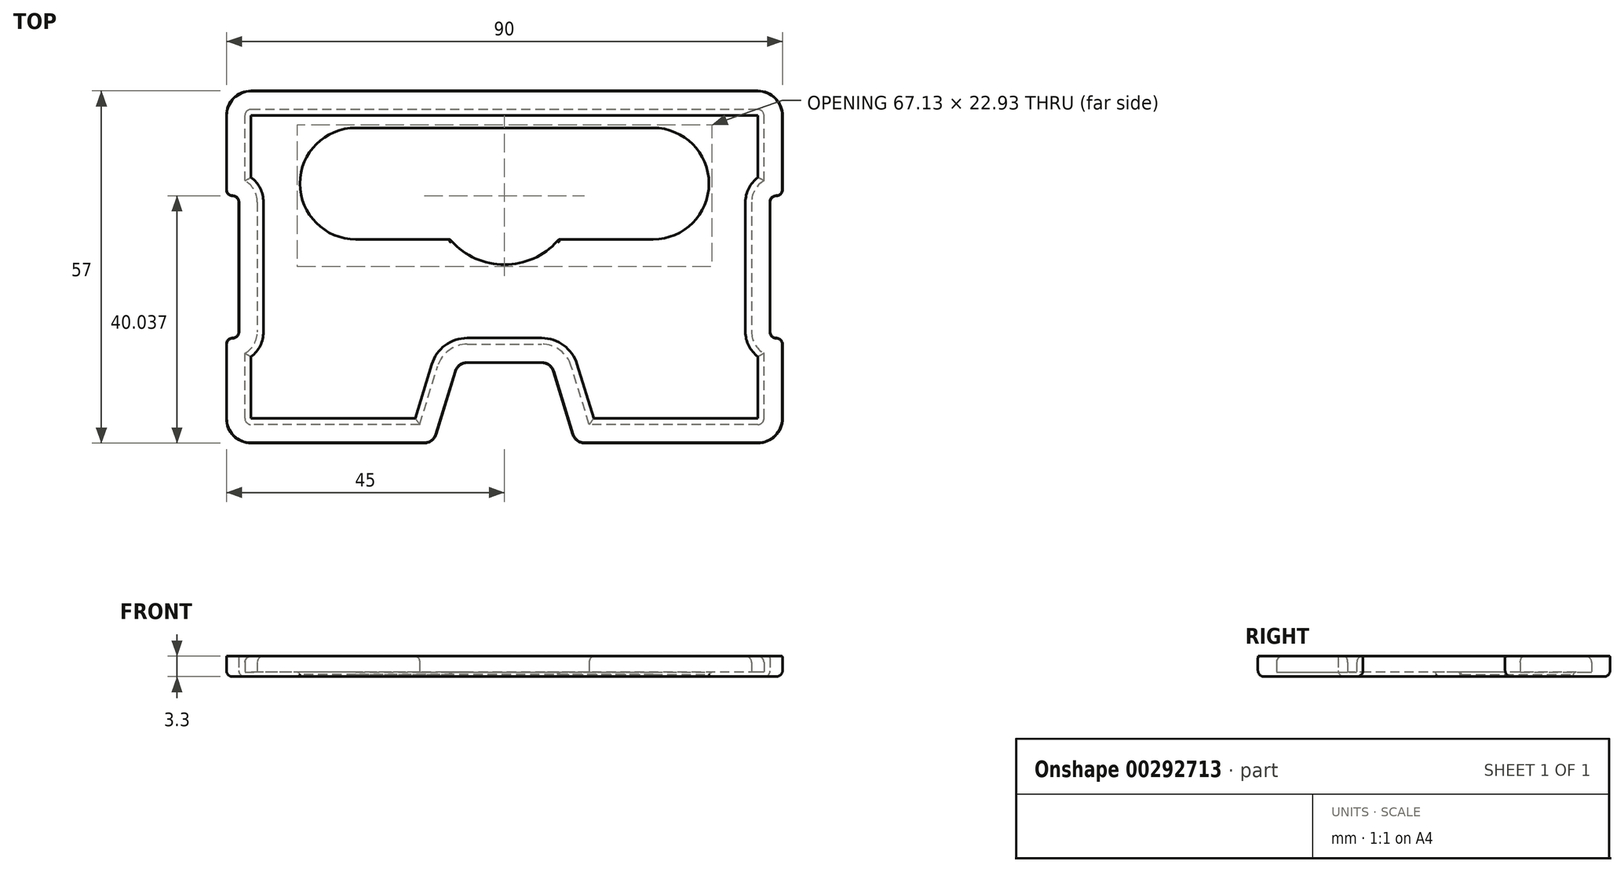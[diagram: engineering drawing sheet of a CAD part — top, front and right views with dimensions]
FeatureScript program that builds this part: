
annotation { "Feature Type Name" : "Feature", "Feature Type Description" : "" }
export const myFeature = defineFeature(function(context is Context, id is Id, definition is map)
    precondition{}
    {
        {
            var Q0;
            Q0=qCreatedBy(makeId("Top.planeOp"),FACE);
            var sketch = newSketch(context, id + "F0", { "sketchPlane" : qUnion([Q0])});
            skLineSegment(sketch, "E0.bottom", {"start": v(41, -28.5) * mm, "end": v(12.98, -28.5) * mm});
            skLineSegment(sketch, "E0.top", {"start": v(41, 28.5) * mm, "end": v(-41, 28.5) * mm});
            skLineSegment(sketch, "E0.left", {"start": v(45, -24.5) * mm, "end": v(45, -12.5) * mm});
            skLineSegment(sketch, "E0.right", {"start": v(-45, -24.5) * mm, "end": v(-45, -12.5) * mm});
            skPoint(sketch, "E0.middle", {"position": v(0, 0) * mm});
            skLineSegment(sketch, "E1.bottom", {"start": v(-44, 11.5) * mm, "end": v(-44, 11.5) * mm});
            skLineSegment(sketch, "E1.top", {"start": v(-44, -11.5) * mm, "end": v(-44, -11.5) * mm});
            skLineSegment(sketch, "E1.right", {"start": v(-43, 10.5) * mm, "end": v(-43, -10.5) * mm});
            skLineSegment(sketch, "E2.bottom", {"start": v(44, 11.5) * mm, "end": v(44, 11.5) * mm});
            skLineSegment(sketch, "E2.top", {"start": v(44, -11.5) * mm, "end": v(44, -11.5) * mm});
            skLineSegment(sketch, "E2.right", {"start": v(43, 10.5) * mm, "end": v(43, -10.5) * mm});
            skLineSegment(sketch, "E3", {"start": v(-45, 12.5) * mm, "end": v(-45, 24.5) * mm});
            skLineSegment(sketch, "E4", {"start": v(45, 12.5) * mm, "end": v(45, 24.5) * mm});
            skLineSegment(sketch, "E5", {"start": v(-12.98, -28.5) * mm, "end": v(-41, -28.5) * mm});
            skPoint(sketch, "E6.visualSharp", {"position": v(45, 28.5) * mm});
            skArc(sketch, "E6.filletArc", {"start": v(45, 24.5) * mm, "mid": v(43.83, 27.33) * mm, "end": v(41, 28.5) * mm});
            skPoint(sketch, "E7.visualSharp", {"position": v(-45, 28.5) * mm});
            skArc(sketch, "E7.filletArc", {"start": v(-41, 28.5) * mm, "mid": v(-43.83, 27.33) * mm, "end": v(-45, 24.5) * mm});
            skPoint(sketch, "E8.visualSharp", {"position": v(-45, -28.5) * mm});
            skArc(sketch, "E8.filletArc", {"start": v(-45, -24.5) * mm, "mid": v(-43.83, -27.33) * mm, "end": v(-41, -28.5) * mm});
            skPoint(sketch, "E9.visualSharp", {"position": v(45, -28.5) * mm});
            skArc(sketch, "E9.filletArc", {"start": v(41, -28.5) * mm, "mid": v(43.83, -27.33) * mm, "end": v(45, -24.5) * mm});
            skPoint(sketch, "E10.visualSharp", {"position": v(-43, 11.5) * mm});
            skArc(sketch, "E10.filletArc", {"start": v(-43, 10.5) * mm, "mid": v(-43.3, 11.2) * mm, "end": v(-44, 11.5) * mm});
            skPoint(sketch, "E11.visualSharp", {"position": v(-43, -11.5) * mm});
            skArc(sketch, "E11.filletArc", {"start": v(-44, -11.5) * mm, "mid": v(-43.3, -11.2) * mm, "end": v(-43, -10.5) * mm});
            skPoint(sketch, "E12.visualSharp", {"position": v(43, 11.5) * mm});
            skArc(sketch, "E12.filletArc", {"start": v(44, 11.5) * mm, "mid": v(43.3, 11.2) * mm, "end": v(43, 10.5) * mm});
            skPoint(sketch, "E13.visualSharp", {"position": v(43, -11.5) * mm});
            skArc(sketch, "E13.filletArc", {"start": v(43, -10.5) * mm, "mid": v(43.3, -11.2) * mm, "end": v(44, -11.5) * mm});
            skPoint(sketch, "E14.visualSharp", {"position": v(-45, 11.5) * mm});
            skArc(sketch, "E14.filletArc", {"start": v(-45, 12.5) * mm, "mid": v(-44.7, 11.8) * mm, "end": v(-44, 11.5) * mm});
            skPoint(sketch, "E15.visualSharp", {"position": v(-45, -11.5) * mm});
            skArc(sketch, "E15.filletArc", {"start": v(-44, -11.5) * mm, "mid": v(-44.7, -11.8) * mm, "end": v(-45, -12.5) * mm});
            skPoint(sketch, "E16.visualSharp", {"position": v(45, 11.5) * mm});
            skArc(sketch, "E16.filletArc", {"start": v(44, 11.5) * mm, "mid": v(44.7, 11.8) * mm, "end": v(45, 12.5) * mm});
            skPoint(sketch, "E17.visualSharp", {"position": v(45, -11.5) * mm});
            skArc(sketch, "E17.filletArc", {"start": v(45, -12.5) * mm, "mid": v(44.7, -11.8) * mm, "end": v(44, -11.5) * mm});
            skLineSegment(sketch, "E18", {"start": v(-11.5, -28.5) * mm, "end": v(-11.5, -15.5) * mm, "construction": true});
            skLineSegment(sketch, "E19", {"start": v(-11.5, -15.5) * mm, "end": v(-7.5, -15.5) * mm, "construction": true});
            skLineSegment(sketch, "E20", {"start": v(-6.02, -15.5) * mm, "end": v(6.02, -15.5) * mm});
            skLineSegment(sketch, "E21", {"start": v(7.5, -15.5) * mm, "end": v(11.5, -15.5) * mm, "construction": true});
            skLineSegment(sketch, "E22", {"start": v(11.5, -15.5) * mm, "end": v(11.5, -28.5) * mm, "construction": true});
            skLineSegment(sketch, "E23", {"start": v(-11.07, -27.09) * mm, "end": v(-7.93, -16.91) * mm});
            skLineSegment(sketch, "E24", {"start": v(11.07, -27.09) * mm, "end": v(7.93, -16.91) * mm});
            skPoint(sketch, "E25.visualSharp", {"position": v(-11.5, -28.5) * mm});
            skArc(sketch, "E25.filletArc", {"start": v(-12.98, -28.5) * mm, "mid": v(-11.79, -28.1) * mm, "end": v(-11.07, -27.09) * mm});
            skPoint(sketch, "E26.visualSharp", {"position": v(11.5, -28.5) * mm});
            skArc(sketch, "E26.filletArc", {"start": v(11.07, -27.09) * mm, "mid": v(11.79, -28.1) * mm, "end": v(12.98, -28.5) * mm});
            skPoint(sketch, "E27.visualSharp", {"position": v(-7.5, -15.5) * mm});
            skArc(sketch, "E27.filletArc", {"start": v(-6.02, -15.5) * mm, "mid": v(-7.21, -15.9) * mm, "end": v(-7.93, -16.91) * mm});
            skPoint(sketch, "E28.visualSharp", {"position": v(7.5, -15.5) * mm});
            skArc(sketch, "E28.filletArc", {"start": v(7.93, -16.91) * mm, "mid": v(7.21, -15.9) * mm, "end": v(6.02, -15.5) * mm});
            skArc(sketch, "E29.11", {"start": v(42.5, 13.66) * mm, "mid": v(41.04, 12.37) * mm, "end": v(40.5, 10.5) * mm, "construction": true});
            skArc(sketch, "E29.20", {"start": v(42.5, 24.5) * mm, "mid": v(42.06, 25.56) * mm, "end": v(41, 26) * mm});
            skArc(sketch, "E30.0", {"start": v(-40, 10.5) * mm, "mid": v(-40.54, 12.5) * mm, "end": v(-42, 13.96) * mm});
            skLineSegment(sketch, "E30.1", {"start": v(-40, 10.5) * mm, "end": v(-40, -10.5) * mm});
            skArc(sketch, "E30.2", {"start": v(-42, -13.96) * mm, "mid": v(-40.54, -12.5) * mm, "end": v(-40, -10.5) * mm});
            skLineSegment(sketch, "E30.3", {"start": v(-42, -24.5) * mm, "end": v(-42, -13.96) * mm});
            skArc(sketch, "E30.4", {"start": v(-42, -24.5) * mm, "mid": v(-41.7, -25.2) * mm, "end": v(-41, -25.5) * mm});
            skLineSegment(sketch, "E30.5", {"start": v(-42, 13.96) * mm, "end": v(-42, 24.5) * mm});
            skLineSegment(sketch, "E30.6", {"start": v(-13.72, -25.5) * mm, "end": v(-41, -25.5) * mm});
            skLineSegment(sketch, "E30.7", {"start": v(-13.72, -25.5) * mm, "end": v(-10.8, -16.03) * mm});
            skArc(sketch, "E30.8", {"start": v(-6.02, -12.5) * mm, "mid": v(-9, -13.48) * mm, "end": v(-10.8, -16.03) * mm});
            skLineSegment(sketch, "E30.9", {"start": v(-6.02, -12.5) * mm, "end": v(6.02, -12.5) * mm});
            skArc(sketch, "E30.10", {"start": v(10.8, -16.03) * mm, "mid": v(9, -13.48) * mm, "end": v(6.02, -12.5) * mm});
            skLineSegment(sketch, "E30.11", {"start": v(13.72, -25.5) * mm, "end": v(10.8, -16.03) * mm});
            skLineSegment(sketch, "E30.12", {"start": v(42, 13.96) * mm, "end": v(42, 24.5) * mm});
            skArc(sketch, "E30.13", {"start": v(42, 24.5) * mm, "mid": v(41.7, 25.2) * mm, "end": v(41, 25.5) * mm});
            skLineSegment(sketch, "E30.14", {"start": v(41, 25.5) * mm, "end": v(-41, 25.5) * mm});
            skArc(sketch, "E30.15", {"start": v(-41, 25.5) * mm, "mid": v(-41.7, 25.2) * mm, "end": v(-42, 24.5) * mm});
            skArc(sketch, "E30.16", {"start": v(42, 13.96) * mm, "mid": v(40.54, 12.5) * mm, "end": v(40, 10.5) * mm});
            skLineSegment(sketch, "E30.17", {"start": v(40, 10.5) * mm, "end": v(40, -10.5) * mm});
            skArc(sketch, "E30.18", {"start": v(40, -10.5) * mm, "mid": v(40.54, -12.5) * mm, "end": v(42, -13.96) * mm});
            skLineSegment(sketch, "E30.19", {"start": v(42, -24.5) * mm, "end": v(42, -13.96) * mm});
            skArc(sketch, "E30.20", {"start": v(41, -25.5) * mm, "mid": v(41.7, -25.2) * mm, "end": v(42, -24.5) * mm});
            skLineSegment(sketch, "E30.21", {"start": v(41, -25.5) * mm, "end": v(13.72, -25.5) * mm});
            skLineSegment(sketch, "E31.bottom", {"start": v(-24.06, 22.5) * mm, "end": v(24.06, 22.5) * mm});
            skLineSegment(sketch, "E31.top", {"start": v(-24.06, 4.5) * mm, "end": v(24.06, 4.5) * mm});
            skLineSegment(sketch, "E31.left", {"start": v(-24.06, 22.5) * mm, "end": v(-24.06, 4.5) * mm, "construction": true});
            skLineSegment(sketch, "E31.right", {"start": v(24.06, 22.5) * mm, "end": v(24.06, 4.5) * mm, "construction": true});
            skCircle(sketch, "E32", {"center": v(-24.06, 13.5) * mm, "radius": 9 * mm});
            skCircle(sketch, "E33", {"center": v(24.06, 13.5) * mm, "radius": 9 * mm});
            skArc(sketch, "E34", {"start": v(-8.83, 4.5) * mm, "mid": v(0, 0.37) * mm, "end": v(8.83, 4.5) * mm});
            skPoint(sketch, "E35", {"position": v(0, 22.5) * mm});
            skLineSegment(sketch, "E36", {"start": v(0, 44.05) * mm, "end": v(0, -36.18) * mm, "construction": true});
            skPoint(sketch, "E37", {"position": v(0, 3.93) * mm});
            skPoint(sketch, "E38", {"position": v(-8.83, 4.5) * mm});
            skPoint(sketch, "E39", {"position": v(8.83, 4.5) * mm});
            skSolve(sketch);
        }
        {
            var Q0;
            Q0=makeQuery(id+"F0.imprint","IMPRINT",FACE,{"disambiguationData":[TD([[makeQuery(id+"F0.imprint","IMPRINT",EDGE,{"derivedFrom":sQuery(id+"F0.wireOp",EDGE,"E0.bottom")}),-1.0]])]});
            extrude(context, id + "F1", {"entities" : qUnion([Q0]), "depth" : 4 * mm, "offsetDistance" : 25 * mm});
        }
        {
            var Q0;
            Q0=makeQuery(id+"F0.imprint","IMPRINT",FACE,{"disambiguationData":[TD([[makeQuery(id+"F0.imprint","IMPRINT",EDGE,{"derivedFrom":sQuery(id+"F0.wireOp",EDGE,"E30.0")}),-1.0]])]});
            extrude(context, id + "F2", {"entities" : qUnion([Q0]), "operationType" : NewBodyOperationType.ADD, "depth" : 0.7 * mm, "offsetDistance" : 25 * mm});
        }
        {
            var Q0;
            Q0=makeQuery(id+"F1.opExtrude","CAP_FACE",FACE,{"disambiguationData":[OSD([sQuery(id+"F0.wireOp",EDGE,"E0.bottom"),sQuery(id+"F0.wireOp",EDGE,"E0.top"),sQuery(id+"F0.wireOp",EDGE,"E0.left"),sQuery(id+"F0.wireOp",EDGE,"E0.right"),sQuery(id+"F0.wireOp",EDGE,"E1.right"),sQuery(id+"F0.wireOp",EDGE,"E2.right"),sQuery(id+"F0.wireOp",EDGE,"E3"),sQuery(id+"F0.wireOp",EDGE,"E4"),sQuery(id+"F0.wireOp",EDGE,"E5"),sQuery(id+"F0.wireOp",EDGE,"E6.filletArc"),sQuery(id+"F0.wireOp",EDGE,"E7.filletArc"),sQuery(id+"F0.wireOp",EDGE,"E8.filletArc"),sQuery(id+"F0.wireOp",EDGE,"E9.filletArc"),sQuery(id+"F0.wireOp",EDGE,"E10.filletArc"),sQuery(id+"F0.wireOp",EDGE,"E11.filletArc"),sQuery(id+"F0.wireOp",EDGE,"E12.filletArc"),sQuery(id+"F0.wireOp",EDGE,"E13.filletArc"),sQuery(id+"F0.wireOp",EDGE,"E14.filletArc"),sQuery(id+"F0.wireOp",EDGE,"E15.filletArc"),sQuery(id+"F0.wireOp",EDGE,"E16.filletArc"),sQuery(id+"F0.wireOp",EDGE,"E17.filletArc"),sQuery(id+"F0.wireOp",EDGE,"E20"),sQuery(id+"F0.wireOp",EDGE,"E23"),sQuery(id+"F0.wireOp",EDGE,"E24"),sQuery(id+"F0.wireOp",EDGE,"E25.filletArc"),sQuery(id+"F0.wireOp",EDGE,"E26.filletArc"),sQuery(id+"F0.wireOp",EDGE,"E27.filletArc"),sQuery(id+"F0.wireOp",EDGE,"E28.filletArc"),sQuery(id+"F0.wireOp",EDGE,"E30.0"),sQuery(id+"F0.wireOp",EDGE,"E30.1"),sQuery(id+"F0.wireOp",EDGE,"E30.2"),sQuery(id+"F0.wireOp",EDGE,"E30.3"),sQuery(id+"F0.wireOp",EDGE,"E30.4"),sQuery(id+"F0.wireOp",EDGE,"E30.5"),sQuery(id+"F0.wireOp",EDGE,"E30.6"),sQuery(id+"F0.wireOp",EDGE,"E30.7"),sQuery(id+"F0.wireOp",EDGE,"E30.8"),sQuery(id+"F0.wireOp",EDGE,"E30.9"),sQuery(id+"F0.wireOp",EDGE,"E30.10"),sQuery(id+"F0.wireOp",EDGE,"E30.11"),sQuery(id+"F0.wireOp",EDGE,"E30.12"),sQuery(id+"F0.wireOp",EDGE,"E30.13"),sQuery(id+"F0.wireOp",EDGE,"E30.14"),sQuery(id+"F0.wireOp",EDGE,"E30.15"),sQuery(id+"F0.wireOp",EDGE,"E30.16"),sQuery(id+"F0.wireOp",EDGE,"E30.17"),sQuery(id+"F0.wireOp",EDGE,"E30.18"),sQuery(id+"F0.wireOp",EDGE,"E30.19"),sQuery(id+"F0.wireOp",EDGE,"E30.20"),sQuery(id+"F0.wireOp",EDGE,"E30.21")])],"isStart":false});
            var sketch = newSketch(context, id + "F3", { "sketchPlane" : qUnion([Q0])});
            skArc(sketch, "E40.0.0", {"start": v(-44, 11.5) * mm, "mid": v(-43.3, 11.2) * mm, "end": v(-43, 10.5) * mm});
            skLineSegment(sketch, "E40.0.1", {"start": v(-43, 10.5) * mm, "end": v(-43, -10.5) * mm});
            skArc(sketch, "E40.0.2", {"start": v(-43, -10.5) * mm, "mid": v(-43.3, -11.2) * mm, "end": v(-44, -11.5) * mm});
            skArc(sketch, "E40.0.3", {"start": v(-44, -11.5) * mm, "mid": v(-44.7, -11.8) * mm, "end": v(-45, -12.5) * mm});
            skLineSegment(sketch, "E40.0.4", {"start": v(-45, -12.5) * mm, "end": v(-45, -24.5) * mm});
            skArc(sketch, "E40.0.5", {"start": v(-45, -24.5) * mm, "mid": v(-43.83, -27.33) * mm, "end": v(-41, -28.5) * mm});
            skLineSegment(sketch, "E40.0.6", {"start": v(-41, -28.5) * mm, "end": v(-12.98, -28.5) * mm});
            skArc(sketch, "E40.0.7", {"start": v(-12.98, -28.5) * mm, "mid": v(-11.79, -28.1) * mm, "end": v(-11.07, -27.09) * mm});
            skLineSegment(sketch, "E40.0.8", {"start": v(-11.07, -27.09) * mm, "end": v(-7.93, -16.91) * mm});
            skArc(sketch, "E40.0.9", {"start": v(-7.93, -16.91) * mm, "mid": v(-7.21, -15.9) * mm, "end": v(-6.02, -15.5) * mm});
            skLineSegment(sketch, "E40.0.10", {"start": v(-6.02, -15.5) * mm, "end": v(6.02, -15.5) * mm});
            skArc(sketch, "E40.0.11", {"start": v(6.02, -15.5) * mm, "mid": v(7.21, -15.9) * mm, "end": v(7.93, -16.91) * mm});
            skLineSegment(sketch, "E40.0.12", {"start": v(7.93, -16.91) * mm, "end": v(11.07, -27.09) * mm});
            skArc(sketch, "E40.0.13", {"start": v(11.07, -27.09) * mm, "mid": v(11.79, -28.1) * mm, "end": v(12.98, -28.5) * mm});
            skLineSegment(sketch, "E40.0.14", {"start": v(12.98, -28.5) * mm, "end": v(41, -28.5) * mm});
            skArc(sketch, "E40.0.15", {"start": v(41, -28.5) * mm, "mid": v(43.83, -27.33) * mm, "end": v(45, -24.5) * mm});
            skLineSegment(sketch, "E40.0.16", {"start": v(45, -24.5) * mm, "end": v(45, -12.5) * mm});
            skArc(sketch, "E40.0.17", {"start": v(45, -12.5) * mm, "mid": v(44.7, -11.8) * mm, "end": v(44, -11.5) * mm});
            skArc(sketch, "E40.0.18", {"start": v(44, -11.5) * mm, "mid": v(43.3, -11.2) * mm, "end": v(43, -10.5) * mm});
            skLineSegment(sketch, "E40.0.19", {"start": v(43, -10.5) * mm, "end": v(43, 10.5) * mm});
            skArc(sketch, "E40.0.20", {"start": v(43, 10.5) * mm, "mid": v(43.3, 11.2) * mm, "end": v(44, 11.5) * mm});
            skArc(sketch, "E40.0.21", {"start": v(44, 11.5) * mm, "mid": v(44.7, 11.8) * mm, "end": v(45, 12.5) * mm});
            skLineSegment(sketch, "E40.0.22", {"start": v(45, 12.5) * mm, "end": v(45, 24.5) * mm});
            skArc(sketch, "E40.0.23", {"start": v(45, 24.5) * mm, "mid": v(43.83, 27.33) * mm, "end": v(41, 28.5) * mm});
            skLineSegment(sketch, "E40.0.24", {"start": v(41, 28.5) * mm, "end": v(-41, 28.5) * mm});
            skArc(sketch, "E40.0.25", {"start": v(-41, 28.5) * mm, "mid": v(-43.83, 27.33) * mm, "end": v(-45, 24.5) * mm});
            skLineSegment(sketch, "E40.0.26", {"start": v(-45, 24.5) * mm, "end": v(-45, 12.5) * mm});
            skArc(sketch, "E40.0.27", {"start": v(-45, 12.5) * mm, "mid": v(-44.7, 11.8) * mm, "end": v(-44, 11.5) * mm});
            skArc(sketch, "E40.1.0", {"start": v(42, -13.96) * mm, "mid": v(40.54, -12.5) * mm, "end": v(40, -10.5) * mm});
            skLineSegment(sketch, "E40.1.1", {"start": v(40, -10.5) * mm, "end": v(40, 10.5) * mm});
            skArc(sketch, "E40.1.2", {"start": v(40, 10.5) * mm, "mid": v(40.54, 12.5) * mm, "end": v(42, 13.96) * mm});
            skLineSegment(sketch, "E40.1.3", {"start": v(42, 13.96) * mm, "end": v(42, 24.5) * mm});
            skArc(sketch, "E40.1.4", {"start": v(42, 24.5) * mm, "mid": v(41.7, 25.2) * mm, "end": v(41, 25.5) * mm});
            skLineSegment(sketch, "E40.1.5", {"start": v(41, 25.5) * mm, "end": v(-41, 25.5) * mm});
            skArc(sketch, "E40.1.6", {"start": v(-41, 25.5) * mm, "mid": v(-41.7, 25.2) * mm, "end": v(-42, 24.5) * mm});
            skLineSegment(sketch, "E40.1.7", {"start": v(-42, 24.5) * mm, "end": v(-42, 13.96) * mm});
            skArc(sketch, "E40.1.8", {"start": v(-42, 13.96) * mm, "mid": v(-40.54, 12.5) * mm, "end": v(-40, 10.5) * mm});
            skLineSegment(sketch, "E40.1.9", {"start": v(-40, 10.5) * mm, "end": v(-40, -10.5) * mm});
            skArc(sketch, "E40.1.10", {"start": v(-40, -10.5) * mm, "mid": v(-40.54, -12.5) * mm, "end": v(-42, -13.96) * mm});
            skLineSegment(sketch, "E40.1.11", {"start": v(-42, -13.96) * mm, "end": v(-42, -24.5) * mm});
            skArc(sketch, "E40.1.12", {"start": v(-42, -24.5) * mm, "mid": v(-41.7, -25.2) * mm, "end": v(-41, -25.5) * mm});
            skLineSegment(sketch, "E40.1.13", {"start": v(-41, -25.5) * mm, "end": v(-13.72, -25.5) * mm});
            skLineSegment(sketch, "E40.1.14", {"start": v(-13.72, -25.5) * mm, "end": v(-10.8, -16.03) * mm});
            skArc(sketch, "E40.1.15", {"start": v(-10.8, -16.03) * mm, "mid": v(-9, -13.48) * mm, "end": v(-6.02, -12.5) * mm});
            skLineSegment(sketch, "E40.1.16", {"start": v(-6.02, -12.5) * mm, "end": v(6.02, -12.5) * mm});
            skArc(sketch, "E40.1.17", {"start": v(6.02, -12.5) * mm, "mid": v(9, -13.48) * mm, "end": v(10.8, -16.03) * mm});
            skLineSegment(sketch, "E40.1.18", {"start": v(10.8, -16.03) * mm, "end": v(13.72, -25.5) * mm});
            skLineSegment(sketch, "E40.1.19", {"start": v(13.72, -25.5) * mm, "end": v(41, -25.5) * mm});
            skArc(sketch, "E40.1.20", {"start": v(41, -25.5) * mm, "mid": v(41.7, -25.2) * mm, "end": v(42, -24.5) * mm});
            skLineSegment(sketch, "E40.1.21", {"start": v(42, -24.5) * mm, "end": v(42, -13.96) * mm});
            skCircle(sketch, "E41.0", {"center": v(24.06, 13.5) * mm, "radius": 9 * mm});
            skLineSegment(sketch, "E41.1", {"start": v(-24.06, 22.5) * mm, "end": v(24.06, 22.5) * mm});
            skCircle(sketch, "E41.2", {"center": v(-24.06, 13.5) * mm, "radius": 9 * mm});
            skLineSegment(sketch, "E41.3", {"start": v(-24.06, 4.5) * mm, "end": v(24.06, 4.5) * mm});
            skArc(sketch, "E42.0", {"start": v(-8.83, 4.5) * mm, "mid": v(0, 0.37) * mm, "end": v(8.83, 4.5) * mm});
            skSolve(sketch);
        }
        {
            var Q0;
            Q0=makeQuery(id+"F3.imprint","IMPRINT",FACE,{"disambiguationData":[TD([[makeQuery(id+"F3.imprint","IMPRINT",EDGE,{"derivedFrom":sQuery(id+"F3.wireOp",EDGE,"E40.0.0")}),-1.0]])]});
            var Q1;
            Q1=makeQuery(id+"F3.imprint","IMPRINT",FACE,{"disambiguationData":[TD([[makeQuery(id+"F3.imprint","IMPRINT",EDGE,{"derivedFrom":sQuery(id+"F3.wireOp",EDGE,"E40.1.0")}),-1.0]])]});
            extrude(context, id + "F4", {"entities" : qUnion([Q0, Q1]), "operationType" : NewBodyOperationType.ADD, "oppositeDirection" : true, "depth" : 0.7 * mm, "offsetDistance" : 25 * mm});
        }
        {
            var Q0;
            Q0=makeQuery(id+"F2.opExtrude","CAP_EDGE",EDGE,{"disambiguationData":[OSD([sQuery(id+"F0.wireOp",EDGE,"E30.1")])],"isStart":false});
            var Q1;
            Q1=makeQuery(id+"F2.opExtrude","CAP_EDGE",EDGE,{"disambiguationData":[OSD([sQuery(id+"F0.wireOp",EDGE,"E30.5")])],"isStart":false});
            var Q2;
            Q2=makeQuery(id+"F2.opExtrude","CAP_EDGE",EDGE,{"disambiguationData":[OSD([sQuery(id+"F0.wireOp",EDGE,"E30.3")])],"isStart":false});
            var Q3;
            Q3=makeQuery(id+"F1.opExtrude","CAP_EDGE",EDGE,{"disambiguationData":[OSD([sQuery(id+"F0.wireOp",EDGE,"E30.9")])],"isStart":false});
            var Q4;
            Q4=makeQuery(id+"F1.opExtrude","CAP_EDGE",EDGE,{"disambiguationData":[OSD([sQuery(id+"F0.wireOp",EDGE,"E30.6")])],"isStart":false});
            var Q5;
            Q5=makeQuery(id+"F1.opExtrude","CAP_EDGE",EDGE,{"disambiguationData":[OSD([sQuery(id+"F0.wireOp",EDGE,"E30.3")])],"isStart":false});
            var Q6;
            Q6=makeQuery(id+"F1.opExtrude","CAP_EDGE",EDGE,{"disambiguationData":[OSD([sQuery(id+"F0.wireOp",EDGE,"E30.1")])],"isStart":false});
            var Q7;
            Q7=makeQuery(id+"F1.opExtrude","CAP_EDGE",EDGE,{"disambiguationData":[OSD([sQuery(id+"F0.wireOp",EDGE,"E30.5")])],"isStart":false});
            var Q8;
            Q8=makeQuery(id+"F2.opExtrude","CAP_EDGE",EDGE,{"disambiguationData":[OSD([sQuery(id+"F0.wireOp",EDGE,"E30.6")])],"isStart":false});
            var Q9;
            Q9=makeQuery(id+"F2.opExtrude","CAP_EDGE",EDGE,{"disambiguationData":[OSD([sQuery(id+"F0.wireOp",EDGE,"E30.9")])],"isStart":false});
            var Q10;
            Q10=makeQuery(id+"F2.opExtrude","CAP_EDGE",EDGE,{"disambiguationData":[OSD([sQuery(id+"F0.wireOp",EDGE,"E30.21")])],"isStart":false});
            var Q11;
            Q11=makeQuery(id+"F2.opExtrude","CAP_EDGE",EDGE,{"disambiguationData":[OSD([sQuery(id+"F0.wireOp",EDGE,"E30.17")])],"isStart":false});
            var Q12;
            Q12=makeQuery(id+"F2.opExtrude","CAP_EDGE",EDGE,{"disambiguationData":[OSD([sQuery(id+"F0.wireOp",EDGE,"E30.14")])],"isStart":false});
            var Q13;
            Q13=makeQuery(id+"F1.opExtrude","CAP_EDGE",EDGE,{"disambiguationData":[OSD([sQuery(id+"F0.wireOp",EDGE,"E30.17")])],"isStart":false});
            var Q14;
            Q14=makeQuery(id+"F1.opExtrude","CAP_EDGE",EDGE,{"disambiguationData":[OSD([sQuery(id+"F0.wireOp",EDGE,"E30.19")])],"isStart":false});
            var Q15;
            Q15=makeQuery(id+"F4.boolean.opBoolean","INTERSECT",EDGE,{"derivedFrom":[makeQuery(id+"F1.opExtrude","SWEPT_FACE",FACE,{"disambiguationData":[OSD([sQuery(id+"F0.wireOp",EDGE,"E30.12")])]}),makeQuery(id+"F4.opExtrude","CAP_FACE",FACE,{"disambiguationData":[OSD([sQuery(id+"F3.wireOp",EDGE,"E40.0.0"),sQuery(id+"F3.wireOp",EDGE,"E40.0.1"),sQuery(id+"F3.wireOp",EDGE,"E40.0.2"),sQuery(id+"F3.wireOp",EDGE,"E40.0.3"),sQuery(id+"F3.wireOp",EDGE,"E40.0.4"),sQuery(id+"F3.wireOp",EDGE,"E40.0.5"),sQuery(id+"F3.wireOp",EDGE,"E40.0.6"),sQuery(id+"F3.wireOp",EDGE,"E40.0.7"),sQuery(id+"F3.wireOp",EDGE,"E40.0.8"),sQuery(id+"F3.wireOp",EDGE,"E40.0.9"),sQuery(id+"F3.wireOp",EDGE,"E40.0.10"),sQuery(id+"F3.wireOp",EDGE,"E40.0.11"),sQuery(id+"F3.wireOp",EDGE,"E40.0.12"),sQuery(id+"F3.wireOp",EDGE,"E40.0.13"),sQuery(id+"F3.wireOp",EDGE,"E40.0.14"),sQuery(id+"F3.wireOp",EDGE,"E40.0.15"),sQuery(id+"F3.wireOp",EDGE,"E40.0.16"),sQuery(id+"F3.wireOp",EDGE,"E40.0.17"),sQuery(id+"F3.wireOp",EDGE,"E40.0.18"),sQuery(id+"F3.wireOp",EDGE,"E40.0.19"),sQuery(id+"F3.wireOp",EDGE,"E40.0.20"),sQuery(id+"F3.wireOp",EDGE,"E40.0.21"),sQuery(id+"F3.wireOp",EDGE,"E40.0.22"),sQuery(id+"F3.wireOp",EDGE,"E40.0.23"),sQuery(id+"F3.wireOp",EDGE,"E40.0.24"),sQuery(id+"F3.wireOp",EDGE,"E40.0.25"),sQuery(id+"F3.wireOp",EDGE,"E40.0.26"),sQuery(id+"F3.wireOp",EDGE,"E40.0.27"),sQuery(id+"F3.wireOp",EDGE,"E41.0"),sQuery(id+"F3.wireOp",EDGE,"E41.1"),sQuery(id+"F3.wireOp",EDGE,"E41.2"),sQuery(id+"F3.wireOp",EDGE,"E41.3"),sQuery(id+"F3.wireOp",EDGE,"E41.4")])],"isStart":false})]});
            var Q16;
            Q16=makeQuery(id+"F4.boolean.opBoolean","INTERSECT",EDGE,{"derivedFrom":[makeQuery(id+"F1.opExtrude","SWEPT_FACE",FACE,{"disambiguationData":[OSD([sQuery(id+"F0.wireOp",EDGE,"E30.17")])]}),makeQuery(id+"F4.opExtrude","CAP_FACE",FACE,{"disambiguationData":[OSD([sQuery(id+"F3.wireOp",EDGE,"E40.0.0"),sQuery(id+"F3.wireOp",EDGE,"E40.0.1"),sQuery(id+"F3.wireOp",EDGE,"E40.0.2"),sQuery(id+"F3.wireOp",EDGE,"E40.0.3"),sQuery(id+"F3.wireOp",EDGE,"E40.0.4"),sQuery(id+"F3.wireOp",EDGE,"E40.0.5"),sQuery(id+"F3.wireOp",EDGE,"E40.0.6"),sQuery(id+"F3.wireOp",EDGE,"E40.0.7"),sQuery(id+"F3.wireOp",EDGE,"E40.0.8"),sQuery(id+"F3.wireOp",EDGE,"E40.0.9"),sQuery(id+"F3.wireOp",EDGE,"E40.0.10"),sQuery(id+"F3.wireOp",EDGE,"E40.0.11"),sQuery(id+"F3.wireOp",EDGE,"E40.0.12"),sQuery(id+"F3.wireOp",EDGE,"E40.0.13"),sQuery(id+"F3.wireOp",EDGE,"E40.0.14"),sQuery(id+"F3.wireOp",EDGE,"E40.0.15"),sQuery(id+"F3.wireOp",EDGE,"E40.0.16"),sQuery(id+"F3.wireOp",EDGE,"E40.0.17"),sQuery(id+"F3.wireOp",EDGE,"E40.0.18"),sQuery(id+"F3.wireOp",EDGE,"E40.0.19"),sQuery(id+"F3.wireOp",EDGE,"E40.0.20"),sQuery(id+"F3.wireOp",EDGE,"E40.0.21"),sQuery(id+"F3.wireOp",EDGE,"E40.0.22"),sQuery(id+"F3.wireOp",EDGE,"E40.0.23"),sQuery(id+"F3.wireOp",EDGE,"E40.0.24"),sQuery(id+"F3.wireOp",EDGE,"E40.0.25"),sQuery(id+"F3.wireOp",EDGE,"E40.0.26"),sQuery(id+"F3.wireOp",EDGE,"E40.0.27"),sQuery(id+"F3.wireOp",EDGE,"E41.0"),sQuery(id+"F3.wireOp",EDGE,"E41.1"),sQuery(id+"F3.wireOp",EDGE,"E41.2"),sQuery(id+"F3.wireOp",EDGE,"E41.3"),sQuery(id+"F3.wireOp",EDGE,"E41.4")])],"isStart":false})]});
            var Q17;
            Q17=makeQuery(id+"F4.boolean.opBoolean","INTERSECT",EDGE,{"derivedFrom":[makeQuery(id+"F1.opExtrude","SWEPT_FACE",FACE,{"disambiguationData":[OSD([sQuery(id+"F0.wireOp",EDGE,"E30.19")])]}),makeQuery(id+"F4.opExtrude","CAP_FACE",FACE,{"disambiguationData":[OSD([sQuery(id+"F3.wireOp",EDGE,"E40.0.0"),sQuery(id+"F3.wireOp",EDGE,"E40.0.1"),sQuery(id+"F3.wireOp",EDGE,"E40.0.2"),sQuery(id+"F3.wireOp",EDGE,"E40.0.3"),sQuery(id+"F3.wireOp",EDGE,"E40.0.4"),sQuery(id+"F3.wireOp",EDGE,"E40.0.5"),sQuery(id+"F3.wireOp",EDGE,"E40.0.6"),sQuery(id+"F3.wireOp",EDGE,"E40.0.7"),sQuery(id+"F3.wireOp",EDGE,"E40.0.8"),sQuery(id+"F3.wireOp",EDGE,"E40.0.9"),sQuery(id+"F3.wireOp",EDGE,"E40.0.10"),sQuery(id+"F3.wireOp",EDGE,"E40.0.11"),sQuery(id+"F3.wireOp",EDGE,"E40.0.12"),sQuery(id+"F3.wireOp",EDGE,"E40.0.13"),sQuery(id+"F3.wireOp",EDGE,"E40.0.14"),sQuery(id+"F3.wireOp",EDGE,"E40.0.15"),sQuery(id+"F3.wireOp",EDGE,"E40.0.16"),sQuery(id+"F3.wireOp",EDGE,"E40.0.17"),sQuery(id+"F3.wireOp",EDGE,"E40.0.18"),sQuery(id+"F3.wireOp",EDGE,"E40.0.19"),sQuery(id+"F3.wireOp",EDGE,"E40.0.20"),sQuery(id+"F3.wireOp",EDGE,"E40.0.21"),sQuery(id+"F3.wireOp",EDGE,"E40.0.22"),sQuery(id+"F3.wireOp",EDGE,"E40.0.23"),sQuery(id+"F3.wireOp",EDGE,"E40.0.24"),sQuery(id+"F3.wireOp",EDGE,"E40.0.25"),sQuery(id+"F3.wireOp",EDGE,"E40.0.26"),sQuery(id+"F3.wireOp",EDGE,"E40.0.27"),sQuery(id+"F3.wireOp",EDGE,"E41.0"),sQuery(id+"F3.wireOp",EDGE,"E41.1"),sQuery(id+"F3.wireOp",EDGE,"E41.2"),sQuery(id+"F3.wireOp",EDGE,"E41.3"),sQuery(id+"F3.wireOp",EDGE,"E41.4")])],"isStart":false})]});
            var Q18;
            Q18=makeQuery(id+"F4.boolean.opBoolean","INTERSECT",EDGE,{"derivedFrom":[makeQuery(id+"F1.opExtrude","SWEPT_FACE",FACE,{"disambiguationData":[OSD([sQuery(id+"F0.wireOp",EDGE,"E30.21")])]}),makeQuery(id+"F4.opExtrude","CAP_FACE",FACE,{"disambiguationData":[OSD([sQuery(id+"F3.wireOp",EDGE,"E40.0.0"),sQuery(id+"F3.wireOp",EDGE,"E40.0.1"),sQuery(id+"F3.wireOp",EDGE,"E40.0.2"),sQuery(id+"F3.wireOp",EDGE,"E40.0.3"),sQuery(id+"F3.wireOp",EDGE,"E40.0.4"),sQuery(id+"F3.wireOp",EDGE,"E40.0.5"),sQuery(id+"F3.wireOp",EDGE,"E40.0.6"),sQuery(id+"F3.wireOp",EDGE,"E40.0.7"),sQuery(id+"F3.wireOp",EDGE,"E40.0.8"),sQuery(id+"F3.wireOp",EDGE,"E40.0.9"),sQuery(id+"F3.wireOp",EDGE,"E40.0.10"),sQuery(id+"F3.wireOp",EDGE,"E40.0.11"),sQuery(id+"F3.wireOp",EDGE,"E40.0.12"),sQuery(id+"F3.wireOp",EDGE,"E40.0.13"),sQuery(id+"F3.wireOp",EDGE,"E40.0.14"),sQuery(id+"F3.wireOp",EDGE,"E40.0.15"),sQuery(id+"F3.wireOp",EDGE,"E40.0.16"),sQuery(id+"F3.wireOp",EDGE,"E40.0.17"),sQuery(id+"F3.wireOp",EDGE,"E40.0.18"),sQuery(id+"F3.wireOp",EDGE,"E40.0.19"),sQuery(id+"F3.wireOp",EDGE,"E40.0.20"),sQuery(id+"F3.wireOp",EDGE,"E40.0.21"),sQuery(id+"F3.wireOp",EDGE,"E40.0.22"),sQuery(id+"F3.wireOp",EDGE,"E40.0.23"),sQuery(id+"F3.wireOp",EDGE,"E40.0.24"),sQuery(id+"F3.wireOp",EDGE,"E40.0.25"),sQuery(id+"F3.wireOp",EDGE,"E40.0.26"),sQuery(id+"F3.wireOp",EDGE,"E40.0.27"),sQuery(id+"F3.wireOp",EDGE,"E41.0"),sQuery(id+"F3.wireOp",EDGE,"E41.1"),sQuery(id+"F3.wireOp",EDGE,"E41.2"),sQuery(id+"F3.wireOp",EDGE,"E41.3"),sQuery(id+"F3.wireOp",EDGE,"E41.4")])],"isStart":false})]});
            var Q19;
            Q19=makeQuery(id+"F4.boolean.opBoolean","INTERSECT",EDGE,{"derivedFrom":[makeQuery(id+"F1.opExtrude","SWEPT_FACE",FACE,{"disambiguationData":[OSD([sQuery(id+"F0.wireOp",EDGE,"E30.9")])]}),makeQuery(id+"F4.opExtrude","CAP_FACE",FACE,{"disambiguationData":[OSD([sQuery(id+"F3.wireOp",EDGE,"E40.0.0"),sQuery(id+"F3.wireOp",EDGE,"E40.0.1"),sQuery(id+"F3.wireOp",EDGE,"E40.0.2"),sQuery(id+"F3.wireOp",EDGE,"E40.0.3"),sQuery(id+"F3.wireOp",EDGE,"E40.0.4"),sQuery(id+"F3.wireOp",EDGE,"E40.0.5"),sQuery(id+"F3.wireOp",EDGE,"E40.0.6"),sQuery(id+"F3.wireOp",EDGE,"E40.0.7"),sQuery(id+"F3.wireOp",EDGE,"E40.0.8"),sQuery(id+"F3.wireOp",EDGE,"E40.0.9"),sQuery(id+"F3.wireOp",EDGE,"E40.0.10"),sQuery(id+"F3.wireOp",EDGE,"E40.0.11"),sQuery(id+"F3.wireOp",EDGE,"E40.0.12"),sQuery(id+"F3.wireOp",EDGE,"E40.0.13"),sQuery(id+"F3.wireOp",EDGE,"E40.0.14"),sQuery(id+"F3.wireOp",EDGE,"E40.0.15"),sQuery(id+"F3.wireOp",EDGE,"E40.0.16"),sQuery(id+"F3.wireOp",EDGE,"E40.0.17"),sQuery(id+"F3.wireOp",EDGE,"E40.0.18"),sQuery(id+"F3.wireOp",EDGE,"E40.0.19"),sQuery(id+"F3.wireOp",EDGE,"E40.0.20"),sQuery(id+"F3.wireOp",EDGE,"E40.0.21"),sQuery(id+"F3.wireOp",EDGE,"E40.0.22"),sQuery(id+"F3.wireOp",EDGE,"E40.0.23"),sQuery(id+"F3.wireOp",EDGE,"E40.0.24"),sQuery(id+"F3.wireOp",EDGE,"E40.0.25"),sQuery(id+"F3.wireOp",EDGE,"E40.0.26"),sQuery(id+"F3.wireOp",EDGE,"E40.0.27"),sQuery(id+"F3.wireOp",EDGE,"E41.0"),sQuery(id+"F3.wireOp",EDGE,"E41.1"),sQuery(id+"F3.wireOp",EDGE,"E41.2"),sQuery(id+"F3.wireOp",EDGE,"E41.3"),sQuery(id+"F3.wireOp",EDGE,"E41.4")])],"isStart":false})]});
            var Q20;
            Q20=makeQuery(id+"F4.boolean.opBoolean","INTERSECT",EDGE,{"derivedFrom":[makeQuery(id+"F1.opExtrude","SWEPT_FACE",FACE,{"disambiguationData":[OSD([sQuery(id+"F0.wireOp",EDGE,"E30.6")])]}),makeQuery(id+"F4.opExtrude","CAP_FACE",FACE,{"disambiguationData":[OSD([sQuery(id+"F3.wireOp",EDGE,"E40.0.0"),sQuery(id+"F3.wireOp",EDGE,"E40.0.1"),sQuery(id+"F3.wireOp",EDGE,"E40.0.2"),sQuery(id+"F3.wireOp",EDGE,"E40.0.3"),sQuery(id+"F3.wireOp",EDGE,"E40.0.4"),sQuery(id+"F3.wireOp",EDGE,"E40.0.5"),sQuery(id+"F3.wireOp",EDGE,"E40.0.6"),sQuery(id+"F3.wireOp",EDGE,"E40.0.7"),sQuery(id+"F3.wireOp",EDGE,"E40.0.8"),sQuery(id+"F3.wireOp",EDGE,"E40.0.9"),sQuery(id+"F3.wireOp",EDGE,"E40.0.10"),sQuery(id+"F3.wireOp",EDGE,"E40.0.11"),sQuery(id+"F3.wireOp",EDGE,"E40.0.12"),sQuery(id+"F3.wireOp",EDGE,"E40.0.13"),sQuery(id+"F3.wireOp",EDGE,"E40.0.14"),sQuery(id+"F3.wireOp",EDGE,"E40.0.15"),sQuery(id+"F3.wireOp",EDGE,"E40.0.16"),sQuery(id+"F3.wireOp",EDGE,"E40.0.17"),sQuery(id+"F3.wireOp",EDGE,"E40.0.18"),sQuery(id+"F3.wireOp",EDGE,"E40.0.19"),sQuery(id+"F3.wireOp",EDGE,"E40.0.20"),sQuery(id+"F3.wireOp",EDGE,"E40.0.21"),sQuery(id+"F3.wireOp",EDGE,"E40.0.22"),sQuery(id+"F3.wireOp",EDGE,"E40.0.23"),sQuery(id+"F3.wireOp",EDGE,"E40.0.24"),sQuery(id+"F3.wireOp",EDGE,"E40.0.25"),sQuery(id+"F3.wireOp",EDGE,"E40.0.26"),sQuery(id+"F3.wireOp",EDGE,"E40.0.27"),sQuery(id+"F3.wireOp",EDGE,"E41.0"),sQuery(id+"F3.wireOp",EDGE,"E41.1"),sQuery(id+"F3.wireOp",EDGE,"E41.2"),sQuery(id+"F3.wireOp",EDGE,"E41.3"),sQuery(id+"F3.wireOp",EDGE,"E41.4")])],"isStart":false})]});
            var Q21;
            Q21=makeQuery(id+"F4.boolean.opBoolean","INTERSECT",EDGE,{"derivedFrom":[makeQuery(id+"F1.opExtrude","SWEPT_FACE",FACE,{"disambiguationData":[OSD([sQuery(id+"F0.wireOp",EDGE,"E30.1")])]}),makeQuery(id+"F4.opExtrude","CAP_FACE",FACE,{"disambiguationData":[OSD([sQuery(id+"F3.wireOp",EDGE,"E40.0.0"),sQuery(id+"F3.wireOp",EDGE,"E40.0.1"),sQuery(id+"F3.wireOp",EDGE,"E40.0.2"),sQuery(id+"F3.wireOp",EDGE,"E40.0.3"),sQuery(id+"F3.wireOp",EDGE,"E40.0.4"),sQuery(id+"F3.wireOp",EDGE,"E40.0.5"),sQuery(id+"F3.wireOp",EDGE,"E40.0.6"),sQuery(id+"F3.wireOp",EDGE,"E40.0.7"),sQuery(id+"F3.wireOp",EDGE,"E40.0.8"),sQuery(id+"F3.wireOp",EDGE,"E40.0.9"),sQuery(id+"F3.wireOp",EDGE,"E40.0.10"),sQuery(id+"F3.wireOp",EDGE,"E40.0.11"),sQuery(id+"F3.wireOp",EDGE,"E40.0.12"),sQuery(id+"F3.wireOp",EDGE,"E40.0.13"),sQuery(id+"F3.wireOp",EDGE,"E40.0.14"),sQuery(id+"F3.wireOp",EDGE,"E40.0.15"),sQuery(id+"F3.wireOp",EDGE,"E40.0.16"),sQuery(id+"F3.wireOp",EDGE,"E40.0.17"),sQuery(id+"F3.wireOp",EDGE,"E40.0.18"),sQuery(id+"F3.wireOp",EDGE,"E40.0.19"),sQuery(id+"F3.wireOp",EDGE,"E40.0.20"),sQuery(id+"F3.wireOp",EDGE,"E40.0.21"),sQuery(id+"F3.wireOp",EDGE,"E40.0.22"),sQuery(id+"F3.wireOp",EDGE,"E40.0.23"),sQuery(id+"F3.wireOp",EDGE,"E40.0.24"),sQuery(id+"F3.wireOp",EDGE,"E40.0.25"),sQuery(id+"F3.wireOp",EDGE,"E40.0.26"),sQuery(id+"F3.wireOp",EDGE,"E40.0.27"),sQuery(id+"F3.wireOp",EDGE,"E41.0"),sQuery(id+"F3.wireOp",EDGE,"E41.1"),sQuery(id+"F3.wireOp",EDGE,"E41.2"),sQuery(id+"F3.wireOp",EDGE,"E41.3"),sQuery(id+"F3.wireOp",EDGE,"E41.4")])],"isStart":false})]});
            fillet(context, id + "F5", {"entities" : qUnion([Q0, Q1, Q2, Q3, Q4, Q5, Q6, Q7, Q8, Q9, Q10, Q11, Q12, Q13, Q14, Q15, Q16, Q17, Q18, Q19, Q20, Q21]), "tangentPropagation" : true, "radius" : 1 * mm, "defaultsChanged" : false, "vertexSettings" : [], "allowEdgeOverflow" : false});
        }
        {
            var Q0;
            Q0=makeQuery(id+"F4.opExtrude","CAP_EDGE",EDGE,{"disambiguationData":[OSD([sQuery(id+"F3.wireOp",EDGE,"E40.0.24")])],"isStart":false});
            var Q1;
            Q1=makeQuery(id+"F1.opExtrude","CAP_EDGE",EDGE,{"disambiguationData":[OSD([sQuery(id+"F0.wireOp",EDGE,"E0.top")])],"isStart":true});
            var Q2;
            Q2=makeQuery(id+"F1.opExtrude","CAP_EDGE",EDGE,{"disambiguationData":[OSD([sQuery(id+"F0.wireOp",EDGE,"E0.top")])],"isStart":false});
            fillet(context, id + "F6", {"entities" : qUnion([Q0, Q1, Q2]), "tangentPropagation" : true, "radius" : 1 * mm, "defaultsChanged" : false, "vertexSettings" : [], "allowEdgeOverflow" : false});
        }
        {
            var Q0;
            {var subQ0=sQuery(id+"F3.wireOp",EDGE,"E41.3");Q0=makeQuery(id+"F4.opExtrude","CAP_EDGE",EDGE,{"disambiguationData":[OSD([subQ0]),TDD([makeQuery(id+"F3.imprint","IMPRINT",EDGE,{"disambiguationData":[TD([[makeQuery(id+"F3.imprint","INTERSECT",VERTEX,{"derivedFrom":[sQuery(id+"F3.wireOp",EDGE,"E41.2"),subQ0]}),-1.0]])],"derivedFrom":subQ0})])],"isStart":false});}
            var Q1;
            {var subQ0=sQuery(id+"F0.wireOp",EDGE,"E31.top");Q1=makeQuery(id+"F2.opExtrude","CAP_EDGE",EDGE,{"disambiguationData":[OSD([subQ0]),TDD([makeQuery(id+"F0.imprint","IMPRINT",EDGE,{"disambiguationData":[TD([[makeQuery(id+"F0.imprint","INTERSECT",VERTEX,{"derivedFrom":[subQ0,sQuery(id+"F0.wireOp",EDGE,"E32")]}),-1.0]])],"derivedFrom":subQ0})])],"isStart":false});}
            var Q2;
            {var subQ0=sQuery(id+"F3.wireOp",EDGE,"E41.3");Q2=makeQuery(id+"F4.opExtrude","CAP_EDGE",EDGE,{"disambiguationData":[OSD([subQ0]),TDD([makeQuery(id+"F3.imprint","IMPRINT",EDGE,{"disambiguationData":[TD([[makeQuery(id+"F3.imprint","INTERSECT",VERTEX,{"derivedFrom":[sQuery(id+"F3.wireOp",EDGE,"E41.0"),subQ0]}),1.0]])],"derivedFrom":subQ0})])],"isStart":true});}
            var Q3;
            Q3=makeQuery(id+"F2.opExtrude","CAP_EDGE",EDGE,{"disambiguationData":[OSD([sQuery(id+"F0.wireOp",EDGE,"E33")])],"isStart":false});
            var Q4;
            {var subQ0=sQuery(id+"F0.wireOp",EDGE,"E31.top");Q4=makeQuery(id+"F2.opExtrude","CAP_EDGE",EDGE,{"disambiguationData":[OSD([subQ0]),TDD([makeQuery(id+"F0.imprint","IMPRINT",EDGE,{"disambiguationData":[TD([[makeQuery(id+"F0.imprint","INTERSECT",VERTEX,{"derivedFrom":[subQ0,sQuery(id+"F0.wireOp",EDGE,"E33")]}),1.0]])],"derivedFrom":subQ0})])],"isStart":false});}
            var Q5;
            {var subQ0=sQuery(id+"F0.wireOp",EDGE,"E31.top");Q5=makeQuery(id+"F2.opExtrude","CAP_EDGE",EDGE,{"disambiguationData":[OSD([subQ0]),TDD([makeQuery(id+"F0.imprint","IMPRINT",EDGE,{"disambiguationData":[TD([[makeQuery(id+"F0.imprint","INTERSECT",VERTEX,{"derivedFrom":[subQ0,sQuery(id+"F0.wireOp",EDGE,"E33")]}),1.0]])],"derivedFrom":subQ0})])],"isStart":true});}
            var Q6;
            {var subQ0=sQuery(id+"F0.wireOp",EDGE,"E34");var subQ1=sQuery(id+"F0.wireOp",EDGE,"E33");var subQ2=sQuery(id+"F0.wireOp",EDGE,"E31.top");var subQ3=sQuery(id+"F0.wireOp",EDGE,"E30.21");var subQ4=sQuery(id+"F0.wireOp",EDGE,"E30.20");var subQ5=sQuery(id+"F0.wireOp",EDGE,"E30.19");var subQ6=sQuery(id+"F0.wireOp",EDGE,"E30.18");var subQ7=sQuery(id+"F0.wireOp",EDGE,"E30.17");var subQ8=sQuery(id+"F0.wireOp",EDGE,"E30.16");var subQ9=sQuery(id+"F0.wireOp",EDGE,"E30.15");var subQ10=sQuery(id+"F0.wireOp",EDGE,"E30.14");var subQ11=sQuery(id+"F0.wireOp",EDGE,"E30.13");var subQ12=sQuery(id+"F0.wireOp",EDGE,"E30.12");var subQ13=sQuery(id+"F0.wireOp",EDGE,"E30.11");var subQ14=sQuery(id+"F0.wireOp",EDGE,"E30.10");var subQ15=sQuery(id+"F0.wireOp",EDGE,"E30.9");var subQ16=sQuery(id+"F0.wireOp",EDGE,"E30.8");var subQ17=sQuery(id+"F0.wireOp",EDGE,"E30.7");var subQ18=sQuery(id+"F0.wireOp",EDGE,"E30.6");var subQ19=sQuery(id+"F0.wireOp",EDGE,"E30.5");var subQ20=sQuery(id+"F0.wireOp",EDGE,"E30.4");var subQ21=sQuery(id+"F0.wireOp",EDGE,"E30.3");var subQ22=sQuery(id+"F0.wireOp",EDGE,"E30.2");var subQ23=sQuery(id+"F0.wireOp",EDGE,"E30.1");var subQ24=sQuery(id+"F0.wireOp",EDGE,"E30.0");Q6=makeQuery(id+"F5.opFillet","BLEND_EDGE",EDGE,{"blendedFrom":[makeQuery(id+"F2.opExtrude","CAP_EDGE",EDGE,{"disambiguationData":[OSD([subQ2]),TDD([makeQuery(id+"F0.imprint","IMPRINT",EDGE,{"disambiguationData":[TD([[makeQuery(id+"F0.imprint","INTERSECT",VERTEX,{"derivedFrom":[subQ2,subQ1]}),1.0]])],"derivedFrom":subQ2})])],"isStart":true}),makeQuery(id+"F2.boolean.opBoolean","MERGE",FACE,{"derivedFrom":[makeQuery(id+"F1.opExtrude","CAP_FACE",FACE,{"disambiguationData":[OSD([sQuery(id+"F0.wireOp",EDGE,"E0.bottom"),sQuery(id+"F0.wireOp",EDGE,"E0.top"),sQuery(id+"F0.wireOp",EDGE,"E0.left"),sQuery(id+"F0.wireOp",EDGE,"E0.right"),sQuery(id+"F0.wireOp",EDGE,"E1.right"),sQuery(id+"F0.wireOp",EDGE,"E2.right"),sQuery(id+"F0.wireOp",EDGE,"E3"),sQuery(id+"F0.wireOp",EDGE,"E4"),sQuery(id+"F0.wireOp",EDGE,"E5"),sQuery(id+"F0.wireOp",EDGE,"E6.filletArc"),sQuery(id+"F0.wireOp",EDGE,"E7.filletArc"),sQuery(id+"F0.wireOp",EDGE,"E8.filletArc"),sQuery(id+"F0.wireOp",EDGE,"E9.filletArc"),sQuery(id+"F0.wireOp",EDGE,"E10.filletArc"),sQuery(id+"F0.wireOp",EDGE,"E11.filletArc"),sQuery(id+"F0.wireOp",EDGE,"E12.filletArc"),sQuery(id+"F0.wireOp",EDGE,"E13.filletArc"),sQuery(id+"F0.wireOp",EDGE,"E14.filletArc"),sQuery(id+"F0.wireOp",EDGE,"E15.filletArc"),sQuery(id+"F0.wireOp",EDGE,"E16.filletArc"),sQuery(id+"F0.wireOp",EDGE,"E17.filletArc"),sQuery(id+"F0.wireOp",EDGE,"E20"),sQuery(id+"F0.wireOp",EDGE,"E23"),sQuery(id+"F0.wireOp",EDGE,"E24"),sQuery(id+"F0.wireOp",EDGE,"E25.filletArc"),sQuery(id+"F0.wireOp",EDGE,"E26.filletArc"),sQuery(id+"F0.wireOp",EDGE,"E27.filletArc"),sQuery(id+"F0.wireOp",EDGE,"E28.filletArc"),subQ24,subQ23,subQ22,subQ21,subQ20,subQ19,subQ18,subQ17,subQ16,subQ15,subQ14,subQ13,subQ12,subQ11,subQ10,subQ9,subQ8,subQ7,subQ6,subQ5,subQ4,subQ3])],"isStart":true}),makeQuery(id+"F2.opExtrude","CAP_FACE",FACE,{"disambiguationData":[OSD([subQ24,subQ23,subQ22,subQ21,subQ20,subQ19,subQ18,subQ17,subQ16,subQ15,subQ14,subQ13,subQ12,subQ11,subQ10,subQ9,subQ8,subQ7,subQ6,subQ5,subQ4,subQ3,sQuery(id+"F0.wireOp",EDGE,"E31.bottom"),subQ2,sQuery(id+"F0.wireOp",EDGE,"E32"),subQ1,subQ0])],"isStart":true})]})],"blendedInto":[makeQuery(id+"F2.boolean.opBoolean","MERGE",FACE,{"derivedFrom":[makeQuery(id+"F1.opExtrude","CAP_FACE",FACE,{"disambiguationData":[OSD([sQuery(id+"F0.wireOp",EDGE,"E0.bottom"),sQuery(id+"F0.wireOp",EDGE,"E0.top"),sQuery(id+"F0.wireOp",EDGE,"E0.left"),sQuery(id+"F0.wireOp",EDGE,"E0.right"),sQuery(id+"F0.wireOp",EDGE,"E1.right"),sQuery(id+"F0.wireOp",EDGE,"E2.right"),sQuery(id+"F0.wireOp",EDGE,"E3"),sQuery(id+"F0.wireOp",EDGE,"E4"),sQuery(id+"F0.wireOp",EDGE,"E5"),sQuery(id+"F0.wireOp",EDGE,"E6.filletArc"),sQuery(id+"F0.wireOp",EDGE,"E7.filletArc"),sQuery(id+"F0.wireOp",EDGE,"E8.filletArc"),sQuery(id+"F0.wireOp",EDGE,"E9.filletArc"),sQuery(id+"F0.wireOp",EDGE,"E10.filletArc"),sQuery(id+"F0.wireOp",EDGE,"E11.filletArc"),sQuery(id+"F0.wireOp",EDGE,"E12.filletArc"),sQuery(id+"F0.wireOp",EDGE,"E13.filletArc"),sQuery(id+"F0.wireOp",EDGE,"E14.filletArc"),sQuery(id+"F0.wireOp",EDGE,"E15.filletArc"),sQuery(id+"F0.wireOp",EDGE,"E16.filletArc"),sQuery(id+"F0.wireOp",EDGE,"E17.filletArc"),sQuery(id+"F0.wireOp",EDGE,"E20"),sQuery(id+"F0.wireOp",EDGE,"E23"),sQuery(id+"F0.wireOp",EDGE,"E24"),sQuery(id+"F0.wireOp",EDGE,"E25.filletArc"),sQuery(id+"F0.wireOp",EDGE,"E26.filletArc"),sQuery(id+"F0.wireOp",EDGE,"E27.filletArc"),sQuery(id+"F0.wireOp",EDGE,"E28.filletArc"),subQ24,subQ23,subQ22,subQ21,subQ20,subQ19,subQ18,subQ17,subQ16,subQ15,subQ14,subQ13,subQ12,subQ11,subQ10,subQ9,subQ8,subQ7,subQ6,subQ5,subQ4,subQ3])],"isStart":true}),makeQuery(id+"F2.opExtrude","CAP_FACE",FACE,{"disambiguationData":[OSD([subQ24,subQ23,subQ22,subQ21,subQ20,subQ19,subQ18,subQ17,subQ16,subQ15,subQ14,subQ13,subQ12,subQ11,subQ10,subQ9,subQ8,subQ7,subQ6,subQ5,subQ4,subQ3,sQuery(id+"F0.wireOp",EDGE,"E31.bottom"),subQ2,sQuery(id+"F0.wireOp",EDGE,"E32"),subQ1,subQ0])],"isStart":true})]})]});}
            fillet(context, id + "F7", {"entities" : qUnion([Q0, Q1, Q2, Q3, Q4, Q5, Q6]), "tangentPropagation" : true, "radius" : 0.5 * mm, "defaultsChanged" : false, "vertexSettings" : [], "allowEdgeOverflow" : false});
        }
        {
            var Q0;
            Q0=makeQuery(id+"F4.opExtrude","CAP_EDGE",EDGE,{"disambiguationData":[OSD([sQuery(id+"F3.wireOp",EDGE,"E41.4")])],"isStart":false});
            var Q1;
            Q1=makeQuery(id+"F4.opExtrude","CAP_EDGE",EDGE,{"disambiguationData":[OSD([sQuery(id+"F3.wireOp",EDGE,"E41.4")])],"isStart":true});
            var Q2;
            Q2=makeQuery(id+"F2.opExtrude","CAP_EDGE",EDGE,{"disambiguationData":[OSD([sQuery(id+"F0.wireOp",EDGE,"E34")])],"isStart":true});
            var Q3;
            Q3=makeQuery(id+"F2.opExtrude","CAP_EDGE",EDGE,{"disambiguationData":[OSD([sQuery(id+"F0.wireOp",EDGE,"E34")])],"isStart":false});
            var Q4;
            Q4=makeQuery(id+"F4.opExtrude","CAP_EDGE",EDGE,{"disambiguationData":[OSD([sQuery(id+"F3.wireOp",EDGE,"E42.0")])],"isStart":true});
            var Q5;
            Q5=makeQuery(id+"F4.opExtrude","CAP_EDGE",EDGE,{"disambiguationData":[OSD([sQuery(id+"F3.wireOp",EDGE,"E42.0")])],"isStart":false});
            fillet(context, id + "F8", {"entities" : qUnion([Q0, Q1, Q2, Q3, Q4, Q5]), "tangentPropagation" : true, "radius" : 0.3 * mm, "defaultsChanged" : false, "vertexSettings" : [], "allowEdgeOverflow" : false});
        }
        {
            var Q0;
            Q0=makeQuery(id+"F3.imprint","IMPRINT",FACE,{"disambiguationData":[TD([[makeQuery(id+"F3.imprint","IMPRINT",EDGE,{"derivedFrom":sQuery(id+"F3.wireOp",EDGE,"E40.0.0")}),-1.0]])]});
            var Q1;
            Q1=makeQuery(id+"F3.imprint","IMPRINT",FACE,{"disambiguationData":[TD([[makeQuery(id+"F3.imprint","IMPRINT",EDGE,{"derivedFrom":sQuery(id+"F3.wireOp",EDGE,"E40.1.0")}),-1.0]])]});
            extrude(context, id + "F9", {"entities" : qUnion([Q0, Q1]), "operationType" : NewBodyOperationType.REMOVE, "oppositeDirection" : true, "depth" : 0.7 * mm, "offsetDistance" : 25 * mm});
        }
    });
